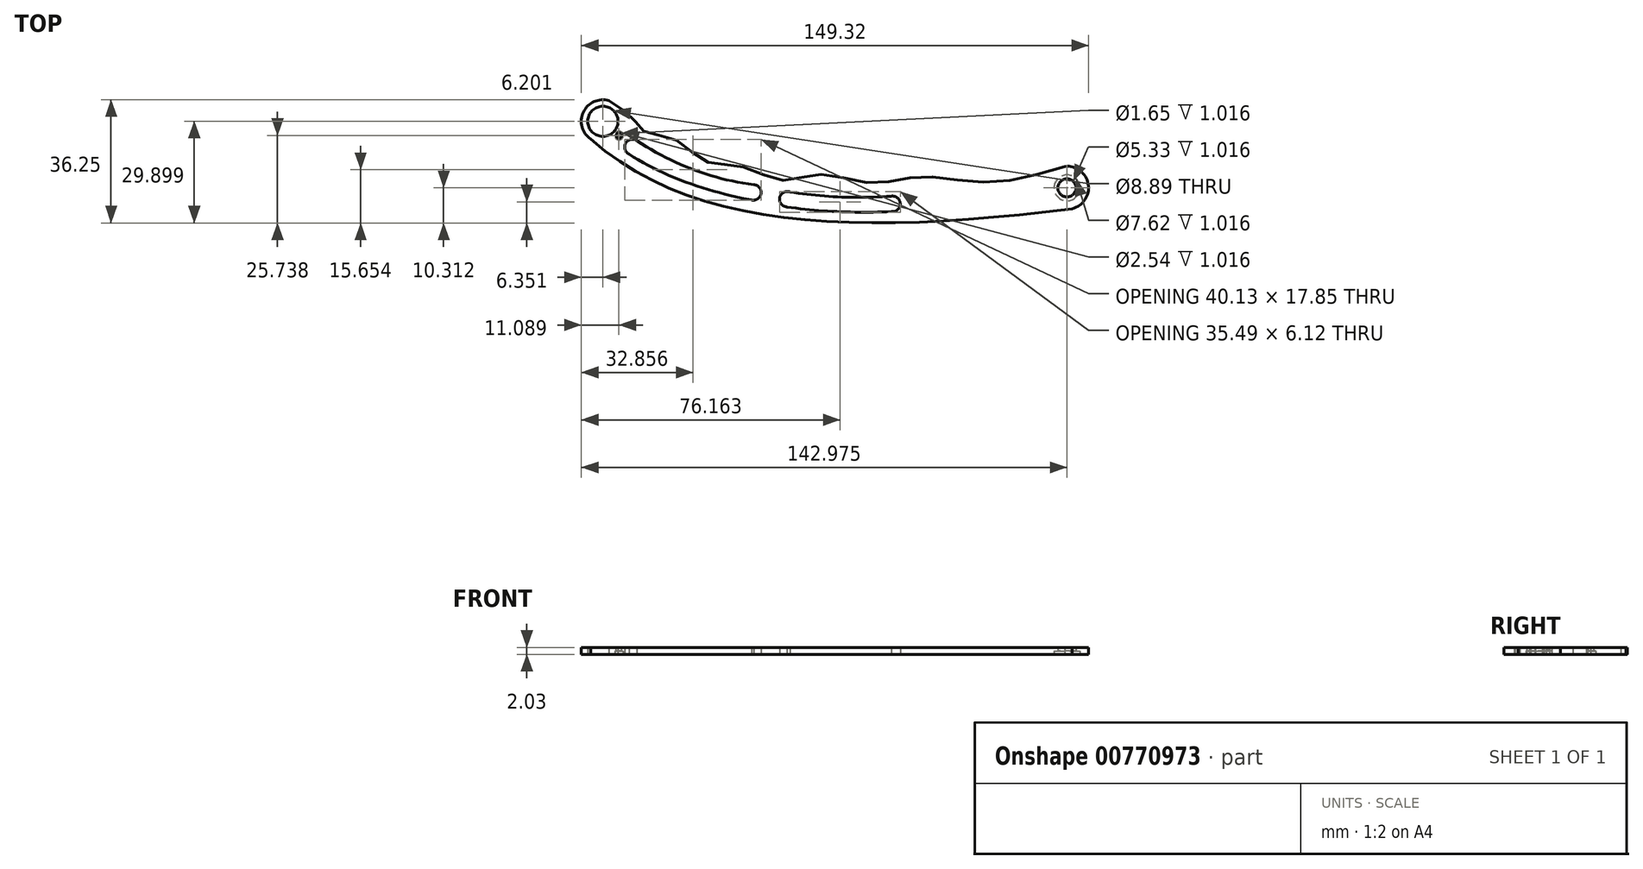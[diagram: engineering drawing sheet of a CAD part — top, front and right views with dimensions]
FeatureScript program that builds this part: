
annotation { "Feature Type Name" : "Feature", "Feature Type Description" : "" }
export const myFeature = defineFeature(function(context is Context, id is Id, definition is map)
    precondition{}
    {
        {
            var Q0;
            Q0=qCreatedBy(makeId("Top.planeOp"),FACE);
            var sketch = newSketch(context, id + "F0", { "sketchPlane" : qUnion([Q0])});
            skArc(sketch, "E0", {"start": v(-20.07, -47.23) * mm, "mid": v(-15.4, -39.99) * mm, "end": v(-22.25, -34.76) * mm});
            skArc(sketch, "E1", {"start": v(-156.48, -15.4) * mm, "mid": v(-164, -18.76) * mm, "end": v(-161.88, -26.72) * mm});
            skFitSpline(sketch, "E2", {"points": [v(-161.88, -26.72) * mm, v(-20.07, -47.23) * mm], "startDerivative": vector(94.28, -83.24) * mm, "endDerivative": vector(181.53, 22.33) * mm});
            skFitSpline(sketch, "E3", {"points": [v(-156.48, -15.4) * mm, v(-149.2, -20.87) * mm, v(-145.9, -24.58) * mm, v(-137.04, -26.85) * mm, v(-127.77, -33.45) * mm, v(-118.5, -34.48) * mm, v(-105.72, -38.8) * mm, v(-94.8, -37.16) * mm, v(-78.93, -39.63) * mm, v(-64.5, -37.78) * mm, v(-45.34, -39.43) * mm, v(-22.25, -34.76) * mm], "startDerivative": vector(108.37, -68.53) * mm, "endDerivative": vector(186.46, 55.9) * mm});
            skCircle(sketch, "E4", {"center": v(-21.65, -41.08) * mm, "radius": 2.67 * mm});
            skCircle(sketch, "E5", {"center": v(-158.27, -21.5) * mm, "radius": 4.45 * mm});
            skPoint(sketch, "E6.orphan", {"position": v(-142.4, -32.8) * mm});
            skArc(sketch, "E7", {"start": v(-148.23, -27.2) * mm, "mid": v(-151.51, -27.86) * mm, "end": v(-150.61, -31.09) * mm});
            skArc(sketch, "E8", {"start": v(-114.46, -44.65) * mm, "mid": v(-111.7, -42.75) * mm, "end": v(-113.78, -40.14) * mm});
            skArc(sketch, "E9", {"start": v(-103.12, -42.3) * mm, "mid": v(-106.2, -43.92) * mm, "end": v(-104.1, -46.7) * mm});
            skArc(sketch, "E10", {"start": v(-73.35, -48.05) * mm, "mid": v(-70.71, -45.78) * mm, "end": v(-73.37, -43.53) * mm});
            skFitSpline(sketch, "E11", {"points": [v(-104.1, -42.13) * mm, v(-72.96, -43.5) * mm], "startDerivative": vector(29.21, -4.98) * mm, "endDerivative": vector(31.97, 2.36) * mm});
            skFitSpline(sketch, "E12", {"points": [v(-104.1, -46.7) * mm, v(-73.35, -48.05) * mm], "startDerivative": vector(30.73, -4.4) * mm, "endDerivative": vector(30.8, 1.47) * mm});
            skFitSpline(sketch, "E13", {"points": [v(-148.4, -27.1) * mm, v(-113.57, -40.16) * mm], "startDerivative": vector(32.12, -21.1) * mm, "endDerivative": vector(38.06, -4.75) * mm});
            skFitSpline(sketch, "E14", {"points": [v(-150.61, -31.09) * mm, v(-114.46, -44.65) * mm], "startDerivative": vector(30.97, -20.7) * mm, "endDerivative": vector(35.39, -6.39) * mm});
            skSolve(sketch);
        }
        {
            var Q0;
            Q0=makeQuery(id+"F0.imprint","IMPRINT",FACE,{"disambiguationData":[TD([[makeQuery(id+"F0.imprint","IMPRINT",EDGE,{"derivedFrom":sQuery(id+"F0.wireOp",EDGE,"E0")}),1.0]])]});
            extrude(context, id + "F1", {"entities" : qUnion([Q0]), "depth" : 2.03 * mm, "offsetDistance" : 25.4 * mm});
        }
        {
            var Q0;
            Q0=makeQuery(id+"F1.opExtrude","CAP_FACE",FACE,{"disambiguationData":[OSD([sQuery(id+"F0.wireOp",EDGE,"E0"),sQuery(id+"F0.wireOp",EDGE,"E1"),sQuery(id+"F0.wireOp",EDGE,"E2"),sQuery(id+"F0.wireOp",EDGE,"E3"),sQuery(id+"F0.wireOp",EDGE,"E4"),sQuery(id+"F0.wireOp",EDGE,"E5"),sQuery(id+"F0.wireOp",EDGE,"E7"),sQuery(id+"F0.wireOp",EDGE,"E8"),sQuery(id+"F0.wireOp",EDGE,"E9"),sQuery(id+"F0.wireOp",EDGE,"E10"),sQuery(id+"F0.wireOp",EDGE,"E11"),sQuery(id+"F0.wireOp",EDGE,"E12"),sQuery(id+"F0.wireOp",EDGE,"E13"),sQuery(id+"F0.wireOp",EDGE,"E14")])],"isStart":false});
            var sketch = newSketch(context, id + "F2", { "sketchPlane" : qUnion([Q0])});
            skCircle(sketch, "E15", {"center": v(-21.65, -41.08) * mm, "radius": 3.81 * mm});
            skSolve(sketch);
        }
        {
            var Q0;
            Q0=makeQuery(id+"F2.imprint","IMPRINT",FACE,{"disambiguationData":[TD([[makeQuery(id+"F2.imprint","IMPRINT",EDGE,{"derivedFrom":sQuery(id+"F2.wireOp",EDGE,"E15")}),1.0]])]});
            extrude(context, id + "F3", {"entities" : qUnion([Q0]), "operationType" : NewBodyOperationType.REMOVE, "oppositeDirection" : true, "depth" : 1.02 * mm, "offsetDistance" : 25.4 * mm});
        }
        {
            var Q0;
            Q0=makeQuery(id+"F1.opExtrude","CAP_FACE",FACE,{"disambiguationData":[OSD([sQuery(id+"F0.wireOp",EDGE,"E0"),sQuery(id+"F0.wireOp",EDGE,"E1"),sQuery(id+"F0.wireOp",EDGE,"E2"),sQuery(id+"F0.wireOp",EDGE,"E3"),sQuery(id+"F0.wireOp",EDGE,"E4"),sQuery(id+"F0.wireOp",EDGE,"E5"),sQuery(id+"F0.wireOp",EDGE,"E7"),sQuery(id+"F0.wireOp",EDGE,"E8"),sQuery(id+"F0.wireOp",EDGE,"E9"),sQuery(id+"F0.wireOp",EDGE,"E10"),sQuery(id+"F0.wireOp",EDGE,"E11"),sQuery(id+"F0.wireOp",EDGE,"E12"),sQuery(id+"F0.wireOp",EDGE,"E13"),sQuery(id+"F0.wireOp",EDGE,"E14")])],"isStart":false});
            var sketch = newSketch(context, id + "F4", { "sketchPlane" : qUnion([Q0])});
            skCircle(sketch, "E16", {"center": v(-153.53, -25.65) * mm, "radius": 0.83 * mm});
            skSolve(sketch);
        }
        {
            var Q0;
            Q0=makeQuery(id+"F4.imprint","IMPRINT",FACE,{"disambiguationData":[TD([[makeQuery(id+"F4.imprint","IMPRINT",EDGE,{"derivedFrom":sQuery(id+"F4.wireOp",EDGE,"E16")}),1.0]])]});
            extrude(context, id + "F5", {"entities" : qUnion([Q0]), "operationType" : NewBodyOperationType.REMOVE, "oppositeDirection" : true, "depth" : 25.4 * mm, "offsetDistance" : 25.4 * mm});
        }
        {
            var Q0;
            Q0=makeQuery(id+"F1.opExtrude","CAP_FACE",FACE,{"disambiguationData":[OSD([sQuery(id+"F0.wireOp",EDGE,"E0"),sQuery(id+"F0.wireOp",EDGE,"E1"),sQuery(id+"F0.wireOp",EDGE,"E2"),sQuery(id+"F0.wireOp",EDGE,"E3"),sQuery(id+"F0.wireOp",EDGE,"E4"),sQuery(id+"F0.wireOp",EDGE,"E5"),sQuery(id+"F0.wireOp",EDGE,"E7"),sQuery(id+"F0.wireOp",EDGE,"E8"),sQuery(id+"F0.wireOp",EDGE,"E9"),sQuery(id+"F0.wireOp",EDGE,"E10"),sQuery(id+"F0.wireOp",EDGE,"E11"),sQuery(id+"F0.wireOp",EDGE,"E12"),sQuery(id+"F0.wireOp",EDGE,"E13"),sQuery(id+"F0.wireOp",EDGE,"E14")])],"isStart":false});
            var sketch = newSketch(context, id + "F6", { "sketchPlane" : qUnion([Q0])});
            skCircle(sketch, "E17", {"center": v(-153.53, -25.65) * mm, "radius": 1.27 * mm});
            skSolve(sketch);
        }
        {
            var Q0;
            Q0=makeQuery(id+"F6.imprint","IMPRINT",FACE,{"disambiguationData":[TD([[makeQuery(id+"F6.imprint","IMPRINT",EDGE,{"derivedFrom":sQuery(id+"F6.wireOp",EDGE,"E17")}),1.0]])]});
            extrude(context, id + "F7", {"entities" : qUnion([Q0]), "operationType" : NewBodyOperationType.REMOVE, "oppositeDirection" : true, "depth" : 1.02 * mm, "offsetDistance" : 25.4 * mm});
        }
        {
            var Q0;
            Q0=makeQuery(id+"F3.boolean.opBoolean","COPY",FACE,{"derivedFrom":makeQuery(id+"F3.opExtrude","CAP_FACE",FACE,{"disambiguationData":[OSD([sQuery(id+"F0.wireOp",EDGE,"E4"),sQuery(id+"F2.wireOp",EDGE,"E15")])],"isStart":false})});
            var Q1;
            Q1=makeQuery(id+"F7.boolean.opBoolean","COPY",FACE,{"derivedFrom":makeQuery(id+"F7.opExtrude","CAP_FACE",FACE,{"disambiguationData":[OSD([sQuery(id+"F4.wireOp",EDGE,"E16"),sQuery(id+"F6.wireOp",EDGE,"E17")])],"isStart":false})});
            var Q2;
            Q2=makeQuery(id+"F1.opExtrude","CAP_FACE",FACE,{"disambiguationData":[OSD([sQuery(id+"F0.wireOp",EDGE,"E0"),sQuery(id+"F0.wireOp",EDGE,"E1"),sQuery(id+"F0.wireOp",EDGE,"E2"),sQuery(id+"F0.wireOp",EDGE,"E3"),sQuery(id+"F0.wireOp",EDGE,"E4"),sQuery(id+"F0.wireOp",EDGE,"E5"),sQuery(id+"F0.wireOp",EDGE,"E7"),sQuery(id+"F0.wireOp",EDGE,"E8"),sQuery(id+"F0.wireOp",EDGE,"E9"),sQuery(id+"F0.wireOp",EDGE,"E10"),sQuery(id+"F0.wireOp",EDGE,"E11"),sQuery(id+"F0.wireOp",EDGE,"E12"),sQuery(id+"F0.wireOp",EDGE,"E13"),sQuery(id+"F0.wireOp",EDGE,"E14")])],"isStart":false});
            extrude(context, id + "F8", {"entities" : qUnion([Q0, Q1]), "operationType" : NewBodyOperationType.ADD, "endBound" : BoundingType.UP_TO_SURFACE, "depth" : 25.4 * mm, "endBoundEntityFace" : qUnion([Q2]), "offsetDistance" : 25.4 * mm});
        }
        {
            var Q0;
            Q0=makeQuery(id+"F1.opExtrude","CAP_FACE",FACE,{"disambiguationData":[OSD([sQuery(id+"F0.wireOp",EDGE,"E0"),sQuery(id+"F0.wireOp",EDGE,"E1"),sQuery(id+"F0.wireOp",EDGE,"E2"),sQuery(id+"F0.wireOp",EDGE,"E3"),sQuery(id+"F0.wireOp",EDGE,"E4"),sQuery(id+"F0.wireOp",EDGE,"E5"),sQuery(id+"F0.wireOp",EDGE,"E7"),sQuery(id+"F0.wireOp",EDGE,"E8"),sQuery(id+"F0.wireOp",EDGE,"E9"),sQuery(id+"F0.wireOp",EDGE,"E10"),sQuery(id+"F0.wireOp",EDGE,"E11"),sQuery(id+"F0.wireOp",EDGE,"E12"),sQuery(id+"F0.wireOp",EDGE,"E13"),sQuery(id+"F0.wireOp",EDGE,"E14")])],"isStart":true});
            var sketch = newSketch(context, id + "F9", { "sketchPlane" : qUnion([Q0])});
            skCircle(sketch, "E18", {"center": v(-21.65, 41.08) * mm, "radius": 3.81 * mm});
            skCircle(sketch, "E19", {"center": v(-153.53, 25.65) * mm, "radius": 1.27 * mm});
            skSolve(sketch);
        }
        {
            var Q0;
            Q0=makeQuery(id+"F9.imprint","IMPRINT",FACE,{"disambiguationData":[TD([[makeQuery(id+"F9.imprint","IMPRINT",EDGE,{"derivedFrom":sQuery(id+"F9.wireOp",EDGE,"E19")}),1.0]])]});
            var Q1;
            Q1=makeQuery(id+"F9.imprint","IMPRINT",FACE,{"disambiguationData":[TD([[makeQuery(id+"F9.imprint","IMPRINT",EDGE,{"derivedFrom":sQuery(id+"F9.wireOp",EDGE,"E18")}),1.0]])]});
            extrude(context, id + "F10", {"entities" : qUnion([Q0, Q1]), "operationType" : NewBodyOperationType.REMOVE, "oppositeDirection" : true, "depth" : 1.02 * mm, "offsetDistance" : 25.4 * mm});
        }
    });
